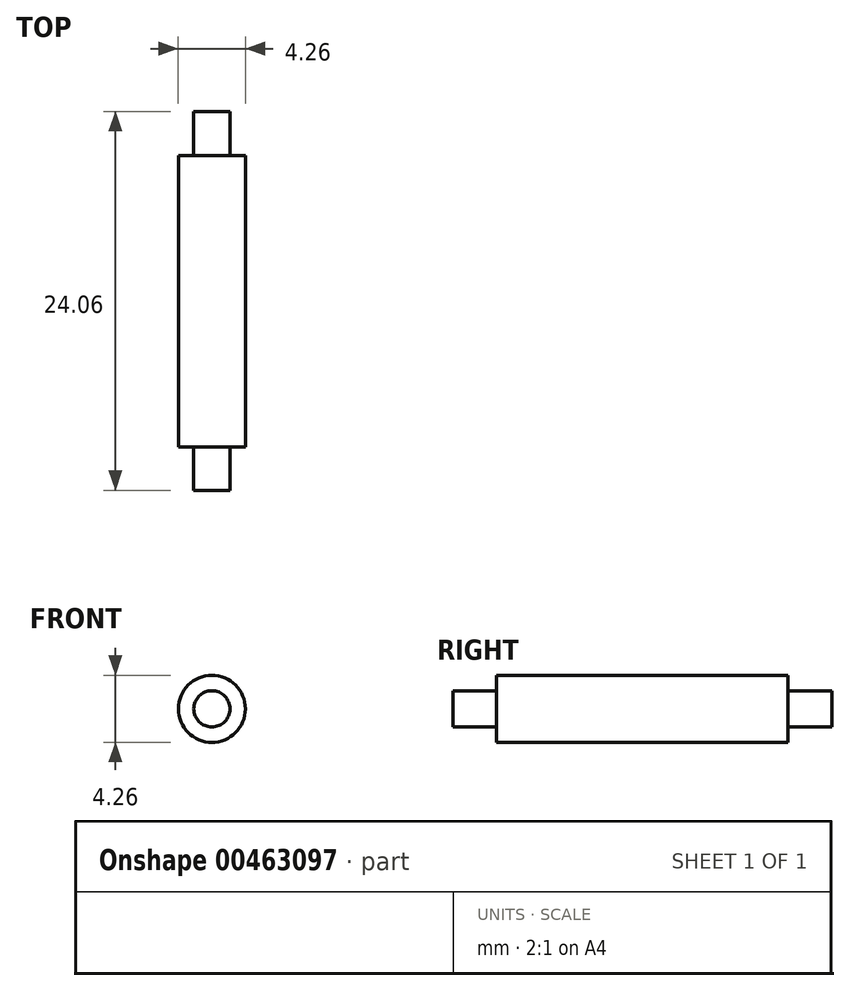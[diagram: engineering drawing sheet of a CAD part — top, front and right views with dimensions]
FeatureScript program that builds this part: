
annotation { "Feature Type Name" : "Feature", "Feature Type Description" : "" }
export const myFeature = defineFeature(function(context is Context, id is Id, definition is map)
    precondition{}
    {
        {
            var Q0;
            Q0=qCreatedBy(makeId("Front.planeOp"),FACE);
            var sketch = newSketch(context, id + "F0", { "sketchPlane" : qUnion([Q0])});
            skCircle(sketch, "E0", {"center": v(0, 0) * mm, "radius": 2.13 * mm});
            skSolve(sketch);
        }
        {
            var Q0;
            Q0=makeQuery(id+"F0.imprint","IMPRINT",FACE,{"disambiguationData":[TD([[makeQuery(id+"F0.imprint","IMPRINT",EDGE,{"derivedFrom":sQuery(id+"F0.wireOp",EDGE,"E0")}),1.0]])]});
            var Q1;
            Q1=sQuery(id+"F0.wireOp",EDGE,"E0");
            extrude(context, id + "F1", {"entities" : qUnion([Q0]), "surfaceEntities" : qUnion([Q1]), "depth" : 18.5 * mm});
        }
        {
            var Q0;
            Q0=qCreatedBy(makeId("Front.planeOp"),FACE);
            var sketch = newSketch(context, id + "F2", { "sketchPlane" : qUnion([Q0])});
            skCircle(sketch, "E1", {"center": v(0, 0) * mm, "radius": 1.15 * mm});
            skSolve(sketch);
        }
        {
            var Q0;
            Q0=makeQuery(id+"F2.imprint","IMPRINT",FACE,{"disambiguationData":[TD([[makeQuery(id+"F2.imprint","IMPRINT",EDGE,{"derivedFrom":sQuery(id+"F2.wireOp",EDGE,"E1")}),1.0]])]});
            extrude(context, id + "F3", {"entities" : qUnion([Q0]), "depth" : -2.8 * mm});
        }
        {
            var Q0;
            Q0=makeQuery(id+"F3.opExtrude","SWEPT_BODY",BODY,{"disambiguationData":[OSD([sQuery(id+"F2.wireOp",EDGE,"E1")])]});
            var Q1;
            Q1=makeQuery(id+"F1.opExtrude","CAP_FACE",FACE,{"disambiguationData":[OSD([sQuery(id+"F0.wireOp",EDGE,"E0")])],"isStart":false});
            mirror(context, id + "F4", {"entities" : qUnion([Q0]), "mirrorPlane" : qUnion([Q1])});
        }
        {
            var Q0;
            Q0=makeQuery(id+"F4.opPattern","COPY",BODY,{"derivedFrom":makeQuery(id+"F3.opExtrude","SWEPT_BODY",BODY,{"disambiguationData":[OSD([sQuery(id+"F2.wireOp",EDGE,"E1")])]}),"instanceName":"1"});
            transform(context, id + "F5", {"entities" : qUnion([Q0]), "transformType" : TransformType.TRANSLATION_3D, "dx" : 0 * mm, "dy" : 18.54 * mm, "dz" : 0 * mm, "makeCopy" : false});
        }
    });
